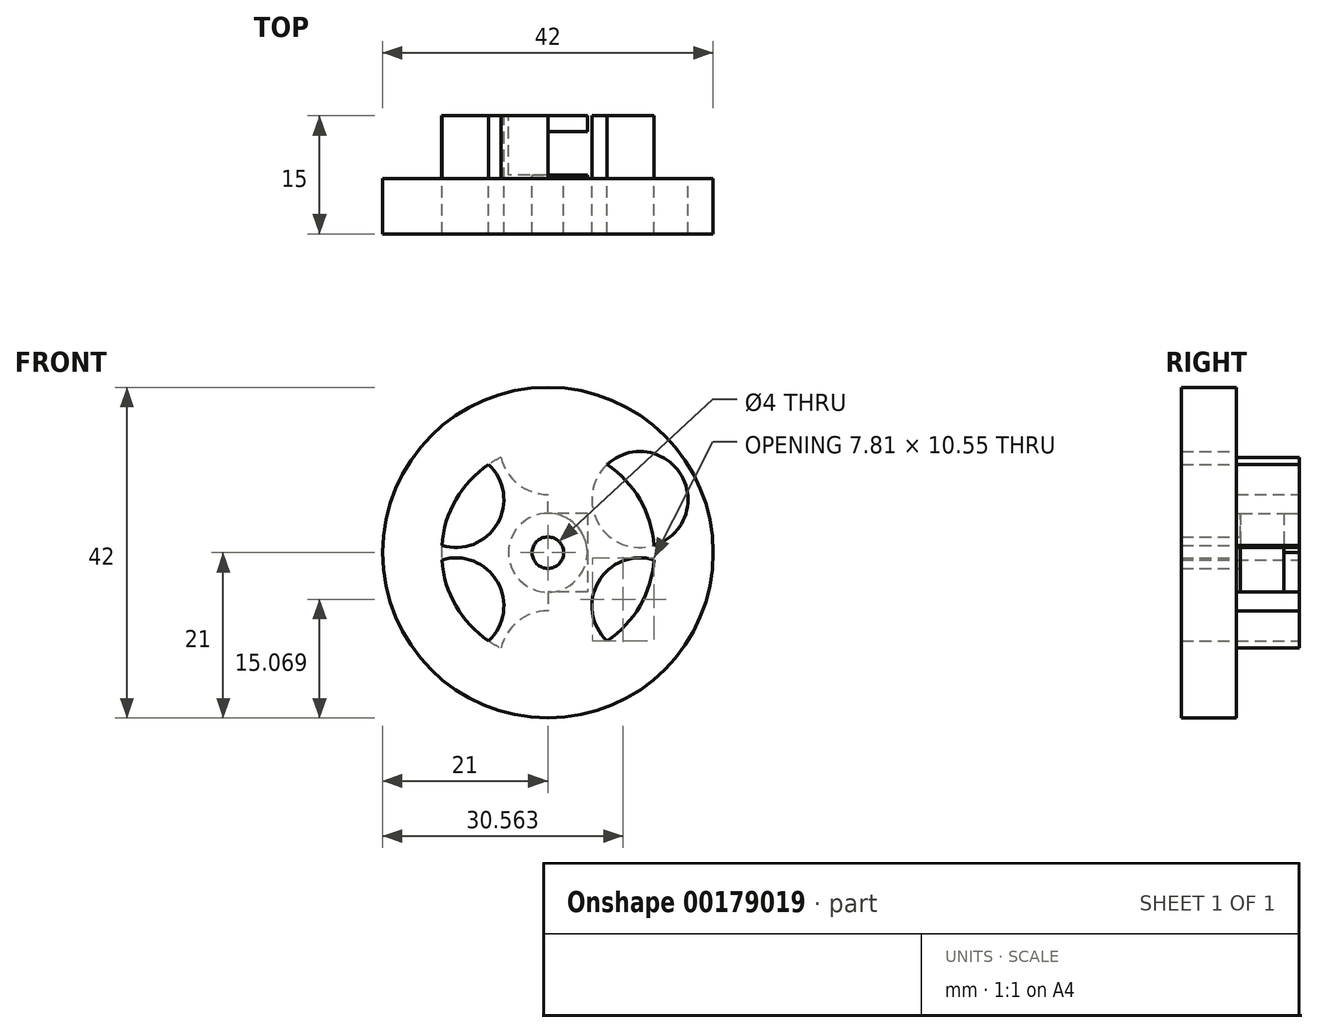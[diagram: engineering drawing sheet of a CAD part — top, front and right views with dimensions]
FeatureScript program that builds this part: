
annotation { "Feature Type Name" : "Feature", "Feature Type Description" : "" }
export const myFeature = defineFeature(function(context is Context, id is Id, definition is map)
    precondition{}
    {
        {
            var Q0;
            Q0=qCreatedBy(makeId("Front.planeOp"),FACE);
            var sketch = newSketch(context, id + "F0", { "sketchPlane" : qUnion([Q0])});
            skCircle(sketch, "E0", {"center": v(0, 0) * mm, "radius": 21 * mm});
            skCircle(sketch, "E1", {"center": v(0, 0) * mm, "radius": 13.5 * mm});
            skCircle(sketch, "E2", {"center": v(0, 13.5) * mm, "radius": 6.1 * mm});
            skLineSegment(sketch, "E3", {"start": v(0, 0) * mm, "end": v(0, 13.5) * mm});
            skLineSegment(sketch, "E4.3.0", {"start": v(0, 0) * mm, "end": v(0, -17.5) * mm});
            skCircle(sketch, "E5", {"center": v(0, 0) * mm, "radius": 5 * mm});
            skCircle(sketch, "E6.1.0", {"center": v(-11.7, 6.75) * mm, "radius": 6.1 * mm});
            skCircle(sketch, "E6.2.0", {"center": v(-11.7, -6.75) * mm, "radius": 6.1 * mm});
            skCircle(sketch, "E6.3.0", {"center": v(0, -13.5) * mm, "radius": 6.1 * mm});
            skCircle(sketch, "E6.4.0", {"center": v(11.7, -6.75) * mm, "radius": 6.1 * mm});
            skCircle(sketch, "E6.5.0", {"center": v(11.7, 6.75) * mm, "radius": 6.1 * mm});
            skSolve(sketch);
        }
        {
            var Q0;
            Q0=qSketchRegion(id+"F0",true);
            var Q1;
            {var subQ3=sQuery(id+"F0.wireOp",EDGE,"tZOFWktZ-ElV9-8rvC-aUia-Pu95TyRWtfmy");var subQ5=sQuery(id+"F0.wireOp",EDGE,"E1");var subQ6=makeQuery(id+"F0.imprint","INTERSECT",VERTEX,{"disambiguationData":[OD(1.0)],"derivedFrom":[subQ5,subQ3]});Q1=makeQuery(id+"F0.imprint","IMPRINT",FACE,{"disambiguationData":[TD([[makeQuery(id+"F0.imprint","IMPRINT",EDGE,{"disambiguationData":[TD([[subQ6,-1.0]])],"derivedFrom":subQ5}),1.0]])]});}
            var Q2;
            {var subQ3=sQuery(id+"F0.wireOp",EDGE,"KCc62wJ9-mbiY-6kxt-bQFC-ecyapfwqHlXu");var subQ5=sQuery(id+"F0.wireOp",EDGE,"E1");var subQ6=makeQuery(id+"F0.imprint","INTERSECT",VERTEX,{"disambiguationData":[OD(1.0)],"derivedFrom":[subQ5,subQ3]});Q2=makeQuery(id+"F0.imprint","IMPRINT",FACE,{"disambiguationData":[TD([[makeQuery(id+"F0.imprint","IMPRINT",EDGE,{"disambiguationData":[TD([[subQ6,-1.0]])],"derivedFrom":subQ5}),1.0]])]});}
            var Q3;
            {var subQ3=sQuery(id+"F0.wireOp",EDGE,"0Yy4USeo-LOO3-cS4v-iVgx-1SsoAEMeRNpn");var subQ5=sQuery(id+"F0.wireOp",EDGE,"E1");var subQ6=makeQuery(id+"F0.imprint","INTERSECT",VERTEX,{"disambiguationData":[OD(1.0)],"derivedFrom":[subQ5,subQ3]});Q3=makeQuery(id+"F0.imprint","IMPRINT",FACE,{"disambiguationData":[TD([[makeQuery(id+"F0.imprint","IMPRINT",EDGE,{"disambiguationData":[TD([[subQ6,-1.0]])],"derivedFrom":subQ5}),1.0]])]});}
            var Q4;
            {var subQ5=sQuery(id+"F0.wireOp",EDGE,"E1");var subQ7=sQuery(id+"F0.wireOp",EDGE,"54YZh0VT-RaSH-f3J3-LX5H-yRfJ3TOlvn7D");var subQ8=makeQuery(id+"F0.imprint","INTERSECT",VERTEX,{"disambiguationData":[OD(0.0)],"derivedFrom":[subQ5,subQ7]});Q4=makeQuery(id+"F0.imprint","IMPRINT",FACE,{"disambiguationData":[TD([[makeQuery(id+"F0.imprint","IMPRINT",EDGE,{"disambiguationData":[TD([[subQ8,-1.0]])],"derivedFrom":subQ5}),1.0]])]});}
            var Q5;
            {var subQ3=sQuery(id+"F0.wireOp",EDGE,"E2");var subQ6=sQuery(id+"F0.wireOp",EDGE,"E1");var subQ9=makeQuery(id+"F0.imprint","INTERSECT",VERTEX,{"disambiguationData":[OD(1.0)],"derivedFrom":[subQ6,subQ3]});Q5=makeQuery(id+"F0.imprint","IMPRINT",FACE,{"disambiguationData":[TD([[makeQuery(id+"F0.imprint","IMPRINT",EDGE,{"disambiguationData":[TD([[subQ9,-1.0]])],"derivedFrom":subQ6}),1.0]])]});}
            var Q6;
            {var subQ0=sQuery(id+"F0.wireOp",EDGE,"E1");var subQ1=makeQuery(id+"F0.imprint","INTERSECT",VERTEX,{"derivedFrom":[subQ0,sQuery(id+"F0.wireOp",EDGE,"E4.3.0")]});Q6=makeQuery(id+"F0.imprint","IMPRINT",FACE,{"disambiguationData":[TD([[makeQuery(id+"F0.imprint","IMPRINT",EDGE,{"disambiguationData":[TD([[subQ1,1.0]])],"derivedFrom":subQ0}),-1.0]])]});}
            var Q7;
            {var subQ0=sQuery(id+"F0.wireOp",EDGE,"E4.3.0");var subQ1=sQuery(id+"F0.wireOp",EDGE,"E1");var subQ2=makeQuery(id+"F0.imprint","INTERSECT",VERTEX,{"derivedFrom":[subQ1,subQ0]});Q7=makeQuery(id+"F0.imprint","IMPRINT",FACE,{"disambiguationData":[TD([[makeQuery(id+"F0.imprint","IMPRINT",EDGE,{"disambiguationData":[TD([[subQ2,-1.0]])],"derivedFrom":subQ1}),1.0]])]});}
            var Q8;
            {var subQ0=sQuery(id+"F0.wireOp",EDGE,"E4.3.0");var subQ1=sQuery(id+"F0.wireOp",EDGE,"E1");var subQ2=makeQuery(id+"F0.imprint","INTERSECT",VERTEX,{"derivedFrom":[subQ1,subQ0]});Q8=makeQuery(id+"F0.imprint","IMPRINT",FACE,{"disambiguationData":[TD([[makeQuery(id+"F0.imprint","IMPRINT",EDGE,{"disambiguationData":[TD([[subQ2,1.0]])],"derivedFrom":subQ1}),1.0]])]});}
            var Q9;
            {var subQ0=sQuery(id+"F0.wireOp",EDGE,"E6.4.0");var subQ1=sQuery(id+"F0.wireOp",EDGE,"E1");var subQ2=makeQuery(id+"F0.imprint","INTERSECT",VERTEX,{"disambiguationData":[OD(0.0)],"derivedFrom":[subQ1,subQ0]});Q9=makeQuery(id+"F0.imprint","IMPRINT",FACE,{"disambiguationData":[TD([[makeQuery(id+"F0.imprint","IMPRINT",EDGE,{"disambiguationData":[TD([[subQ2,-1.0]])],"derivedFrom":subQ1}),-1.0]])]});}
            var Q10;
            {var subQ0=sQuery(id+"F0.wireOp",EDGE,"E6.5.0");var subQ1=sQuery(id+"F0.wireOp",EDGE,"E1");var subQ16=makeQuery(id+"F0.imprint","INTERSECT",VERTEX,{"disambiguationData":[OD(0.0)],"derivedFrom":[subQ1,subQ0]});Q10=makeQuery(id+"F0.imprint","IMPRINT",FACE,{"disambiguationData":[TD([[makeQuery(id+"F0.imprint","IMPRINT",EDGE,{"disambiguationData":[TD([[subQ16,-1.0]])],"derivedFrom":subQ1}),1.0]])]});}
            var Q11;
            {var subQ0=sQuery(id+"F0.wireOp",EDGE,"E4.3.0");var subQ1=sQuery(id+"F0.wireOp",EDGE,"E3");var subQ2=makeQuery(id+"F0.imprint","INTERSECT",VERTEX,{"derivedFrom":[subQ1,subQ0]});Q11=makeQuery(id+"F0.imprint","IMPRINT",FACE,{"disambiguationData":[TD([[makeQuery(id+"F0.imprint","IMPRINT",EDGE,{"disambiguationData":[TD([[subQ2,-1.0]])],"derivedFrom":subQ1}),-1.0]])]});}
            var Q12;
            {var subQ0=sQuery(id+"F0.wireOp",EDGE,"E4.3.0");var subQ1=sQuery(id+"F0.wireOp",EDGE,"E3");var subQ2=makeQuery(id+"F0.imprint","INTERSECT",VERTEX,{"derivedFrom":[subQ1,subQ0]});Q12=makeQuery(id+"F0.imprint","IMPRINT",FACE,{"disambiguationData":[TD([[makeQuery(id+"F0.imprint","IMPRINT",EDGE,{"disambiguationData":[TD([[subQ2,-1.0]])],"derivedFrom":subQ1}),1.0]])]});}
            var Q13;
            {var subQ0=sQuery(id+"F0.wireOp",EDGE,"E6.2.0");var subQ1=sQuery(id+"F0.wireOp",EDGE,"E1");var subQ2=makeQuery(id+"F0.imprint","INTERSECT",VERTEX,{"disambiguationData":[OD(0.0)],"derivedFrom":[subQ1,subQ0]});Q13=makeQuery(id+"F0.imprint","IMPRINT",FACE,{"disambiguationData":[TD([[makeQuery(id+"F0.imprint","IMPRINT",EDGE,{"disambiguationData":[TD([[subQ2,-1.0]])],"derivedFrom":subQ1}),-1.0]])]});}
            var Q14;
            {var subQ0=sQuery(id+"F0.wireOp",EDGE,"E6.1.0");var subQ1=sQuery(id+"F0.wireOp",EDGE,"E1");var subQ2=makeQuery(id+"F0.imprint","INTERSECT",VERTEX,{"disambiguationData":[OD(0.0)],"derivedFrom":[subQ1,subQ0]});Q14=makeQuery(id+"F0.imprint","IMPRINT",FACE,{"disambiguationData":[TD([[makeQuery(id+"F0.imprint","IMPRINT",EDGE,{"disambiguationData":[TD([[subQ2,-1.0]])],"derivedFrom":subQ1}),-1.0]])]});}
            var Q15;
            {var subQ0=sQuery(id+"F0.wireOp",EDGE,"E1");var subQ1=makeQuery(id+"F0.imprint","INTERSECT",VERTEX,{"derivedFrom":[subQ0,sQuery(id+"F0.wireOp",EDGE,"E3")]});Q15=makeQuery(id+"F0.imprint","IMPRINT",FACE,{"disambiguationData":[TD([[makeQuery(id+"F0.imprint","IMPRINT",EDGE,{"disambiguationData":[TD([[subQ1,1.0]])],"derivedFrom":subQ0}),-1.0]])]});}
            var Q16;
            {var subQ0=sQuery(id+"F0.wireOp",EDGE,"E3");var subQ1=sQuery(id+"F0.wireOp",EDGE,"E1");var subQ2=makeQuery(id+"F0.imprint","INTERSECT",VERTEX,{"derivedFrom":[subQ1,subQ0]});Q16=makeQuery(id+"F0.imprint","IMPRINT",FACE,{"disambiguationData":[TD([[makeQuery(id+"F0.imprint","IMPRINT",EDGE,{"disambiguationData":[TD([[subQ2,-1.0]])],"derivedFrom":subQ1}),1.0]])]});}
            var Q17;
            {var subQ0=sQuery(id+"F0.wireOp",EDGE,"E3");var subQ1=sQuery(id+"F0.wireOp",EDGE,"E1");var subQ2=makeQuery(id+"F0.imprint","INTERSECT",VERTEX,{"derivedFrom":[subQ1,subQ0]});Q17=makeQuery(id+"F0.imprint","IMPRINT",FACE,{"disambiguationData":[TD([[makeQuery(id+"F0.imprint","IMPRINT",EDGE,{"disambiguationData":[TD([[subQ2,1.0]])],"derivedFrom":subQ1}),1.0]])]});}
            var Q18;
            {var subQ0=sQuery(id+"F0.wireOp",EDGE,"E6.5.0");var subQ1=sQuery(id+"F0.wireOp",EDGE,"E1");var subQ2=makeQuery(id+"F0.imprint","INTERSECT",VERTEX,{"disambiguationData":[OD(0.0)],"derivedFrom":[subQ1,subQ0]});Q18=makeQuery(id+"F0.imprint","IMPRINT",FACE,{"disambiguationData":[TD([[makeQuery(id+"F0.imprint","IMPRINT",EDGE,{"disambiguationData":[TD([[subQ2,1.0]])],"derivedFrom":subQ1}),1.0]])]});}
            var Q19;
            {var subQ0=sQuery(id+"F0.wireOp",EDGE,"E6.5.0");var subQ1=sQuery(id+"F0.wireOp",EDGE,"E1");var subQ2=makeQuery(id+"F0.imprint","INTERSECT",VERTEX,{"disambiguationData":[OD(0.0)],"derivedFrom":[subQ1,subQ0]});Q19=makeQuery(id+"F0.imprint","IMPRINT",FACE,{"disambiguationData":[TD([[makeQuery(id+"F0.imprint","IMPRINT",EDGE,{"disambiguationData":[TD([[subQ2,1.0]])],"derivedFrom":subQ1}),-1.0]])]});}
            extrude(context, id + "F1", {"entities" : qUnion([Q0, Q1, Q2, Q3, Q4, Q5, Q6, Q7, Q8, Q9, Q10, Q11, Q12, Q13, Q14, Q15, Q16, Q17, Q18, Q19]), "depth" : 15 * mm});
        }
        {
            var Q0;
            {var subQ0=sQuery(id+"F0.wireOp",EDGE,"E6.5.0");var subQ1=sQuery(id+"F0.wireOp",EDGE,"E1");var subQ2=makeQuery(id+"F0.imprint","INTERSECT",VERTEX,{"disambiguationData":[OD(0.0)],"derivedFrom":[subQ1,subQ0]});Q0=makeQuery(id+"F0.imprint","IMPRINT",FACE,{"disambiguationData":[TD([[makeQuery(id+"F0.imprint","IMPRINT",EDGE,{"disambiguationData":[TD([[subQ2,1.0]])],"derivedFrom":subQ1}),1.0]])]});}
            var Q1;
            {var subQ0=sQuery(id+"F0.wireOp",EDGE,"E6.5.0");var subQ1=sQuery(id+"F0.wireOp",EDGE,"E1");var subQ2=makeQuery(id+"F0.imprint","INTERSECT",VERTEX,{"disambiguationData":[OD(0.0)],"derivedFrom":[subQ1,subQ0]});Q1=makeQuery(id+"F0.imprint","IMPRINT",FACE,{"disambiguationData":[TD([[makeQuery(id+"F0.imprint","IMPRINT",EDGE,{"disambiguationData":[TD([[subQ2,1.0]])],"derivedFrom":subQ1}),-1.0]])]});}
            var Q2;
            {var subQ0=sQuery(id+"F0.wireOp",EDGE,"E6.4.0");var subQ1=sQuery(id+"F0.wireOp",EDGE,"E1");var subQ2=makeQuery(id+"F0.imprint","INTERSECT",VERTEX,{"disambiguationData":[OD(0.0)],"derivedFrom":[subQ1,subQ0]});Q2=makeQuery(id+"F0.imprint","IMPRINT",FACE,{"disambiguationData":[TD([[makeQuery(id+"F0.imprint","IMPRINT",EDGE,{"disambiguationData":[TD([[subQ2,-1.0]])],"derivedFrom":subQ1}),-1.0]])]});}
            var Q3;
            {var subQ0=sQuery(id+"F0.wireOp",EDGE,"E6.4.0");var subQ1=sQuery(id+"F0.wireOp",EDGE,"E1");var subQ2=makeQuery(id+"F0.imprint","INTERSECT",VERTEX,{"disambiguationData":[OD(0.0)],"derivedFrom":[subQ1,subQ0]});Q3=makeQuery(id+"F0.imprint","IMPRINT",FACE,{"disambiguationData":[TD([[makeQuery(id+"F0.imprint","IMPRINT",EDGE,{"disambiguationData":[TD([[subQ2,-1.0]])],"derivedFrom":subQ1}),1.0]])]});}
            var Q4;
            {var subQ0=sQuery(id+"F0.wireOp",EDGE,"E4.3.0");var subQ1=sQuery(id+"F0.wireOp",EDGE,"E1");var subQ2=makeQuery(id+"F0.imprint","INTERSECT",VERTEX,{"derivedFrom":[subQ1,subQ0]});Q4=makeQuery(id+"F0.imprint","IMPRINT",FACE,{"disambiguationData":[TD([[makeQuery(id+"F0.imprint","IMPRINT",EDGE,{"disambiguationData":[TD([[subQ2,-1.0]])],"derivedFrom":subQ1}),1.0]])]});}
            var Q5;
            {var subQ0=sQuery(id+"F0.wireOp",EDGE,"E1");var subQ1=makeQuery(id+"F0.imprint","INTERSECT",VERTEX,{"derivedFrom":[subQ0,sQuery(id+"F0.wireOp",EDGE,"E4.3.0")]});Q5=makeQuery(id+"F0.imprint","IMPRINT",FACE,{"disambiguationData":[TD([[makeQuery(id+"F0.imprint","IMPRINT",EDGE,{"disambiguationData":[TD([[subQ1,1.0]])],"derivedFrom":subQ0}),-1.0]])]});}
            var Q6;
            {var subQ0=sQuery(id+"F0.wireOp",EDGE,"E4.3.0");var subQ1=sQuery(id+"F0.wireOp",EDGE,"E1");var subQ2=makeQuery(id+"F0.imprint","INTERSECT",VERTEX,{"derivedFrom":[subQ1,subQ0]});Q6=makeQuery(id+"F0.imprint","IMPRINT",FACE,{"disambiguationData":[TD([[makeQuery(id+"F0.imprint","IMPRINT",EDGE,{"disambiguationData":[TD([[subQ2,1.0]])],"derivedFrom":subQ1}),1.0]])]});}
            var Q7;
            {var subQ0=sQuery(id+"F0.wireOp",EDGE,"E6.2.0");var subQ1=sQuery(id+"F0.wireOp",EDGE,"E1");var subQ2=makeQuery(id+"F0.imprint","INTERSECT",VERTEX,{"disambiguationData":[OD(0.0)],"derivedFrom":[subQ1,subQ0]});Q7=makeQuery(id+"F0.imprint","IMPRINT",FACE,{"disambiguationData":[TD([[makeQuery(id+"F0.imprint","IMPRINT",EDGE,{"disambiguationData":[TD([[subQ2,-1.0]])],"derivedFrom":subQ1}),1.0]])]});}
            var Q8;
            {var subQ0=sQuery(id+"F0.wireOp",EDGE,"E6.2.0");var subQ1=sQuery(id+"F0.wireOp",EDGE,"E1");var subQ2=makeQuery(id+"F0.imprint","INTERSECT",VERTEX,{"disambiguationData":[OD(0.0)],"derivedFrom":[subQ1,subQ0]});Q8=makeQuery(id+"F0.imprint","IMPRINT",FACE,{"disambiguationData":[TD([[makeQuery(id+"F0.imprint","IMPRINT",EDGE,{"disambiguationData":[TD([[subQ2,-1.0]])],"derivedFrom":subQ1}),-1.0]])]});}
            var Q9;
            {var subQ0=sQuery(id+"F0.wireOp",EDGE,"E6.1.0");var subQ1=sQuery(id+"F0.wireOp",EDGE,"E1");var subQ2=makeQuery(id+"F0.imprint","INTERSECT",VERTEX,{"disambiguationData":[OD(0.0)],"derivedFrom":[subQ1,subQ0]});Q9=makeQuery(id+"F0.imprint","IMPRINT",FACE,{"disambiguationData":[TD([[makeQuery(id+"F0.imprint","IMPRINT",EDGE,{"disambiguationData":[TD([[subQ2,-1.0]])],"derivedFrom":subQ1}),1.0]])]});}
            var Q10;
            {var subQ0=sQuery(id+"F0.wireOp",EDGE,"E6.1.0");var subQ1=sQuery(id+"F0.wireOp",EDGE,"E1");var subQ2=makeQuery(id+"F0.imprint","INTERSECT",VERTEX,{"disambiguationData":[OD(0.0)],"derivedFrom":[subQ1,subQ0]});Q10=makeQuery(id+"F0.imprint","IMPRINT",FACE,{"disambiguationData":[TD([[makeQuery(id+"F0.imprint","IMPRINT",EDGE,{"disambiguationData":[TD([[subQ2,-1.0]])],"derivedFrom":subQ1}),-1.0]])]});}
            var Q11;
            {var subQ0=sQuery(id+"F0.wireOp",EDGE,"E3");var subQ1=sQuery(id+"F0.wireOp",EDGE,"E1");var subQ2=makeQuery(id+"F0.imprint","INTERSECT",VERTEX,{"derivedFrom":[subQ1,subQ0]});Q11=makeQuery(id+"F0.imprint","IMPRINT",FACE,{"disambiguationData":[TD([[makeQuery(id+"F0.imprint","IMPRINT",EDGE,{"disambiguationData":[TD([[subQ2,-1.0]])],"derivedFrom":subQ1}),1.0]])]});}
            var Q12;
            {var subQ0=sQuery(id+"F0.wireOp",EDGE,"E3");var subQ1=sQuery(id+"F0.wireOp",EDGE,"E1");var subQ2=makeQuery(id+"F0.imprint","INTERSECT",VERTEX,{"derivedFrom":[subQ1,subQ0]});Q12=makeQuery(id+"F0.imprint","IMPRINT",FACE,{"disambiguationData":[TD([[makeQuery(id+"F0.imprint","IMPRINT",EDGE,{"disambiguationData":[TD([[subQ2,1.0]])],"derivedFrom":subQ1}),1.0]])]});}
            var Q13;
            {var subQ0=sQuery(id+"F0.wireOp",EDGE,"E1");var subQ1=makeQuery(id+"F0.imprint","INTERSECT",VERTEX,{"derivedFrom":[subQ0,sQuery(id+"F0.wireOp",EDGE,"E3")]});Q13=makeQuery(id+"F0.imprint","IMPRINT",FACE,{"disambiguationData":[TD([[makeQuery(id+"F0.imprint","IMPRINT",EDGE,{"disambiguationData":[TD([[subQ1,1.0]])],"derivedFrom":subQ0}),-1.0]])]});}
            extrude(context, id + "F2", {"entities" : qUnion([Q0, Q1, Q2, Q3, Q4, Q5, Q6, Q7, Q8, Q9, Q10, Q11, Q12, Q13]), "operationType" : NewBodyOperationType.REMOVE, "depth" : 8 * mm});
        }
        {
            var Q0;
            Q0=makeQuery(id+"F1.opExtrude","CAP_FACE",FACE,{"disambiguationData":[OSD([sQuery(id+"F0.wireOp",EDGE,"E0")])],"isStart":true});
            var sketch = newSketch(context, id + "F3", { "sketchPlane" : qUnion([Q0])});
            skLineSegment(sketch, "E7.bottom", {"start": v(-5, 5) * mm, "end": v(5, 5) * mm});
            skLineSegment(sketch, "E7.top", {"start": v(-5, -5) * mm, "end": v(5, -5) * mm});
            skLineSegment(sketch, "E7.left", {"start": v(-5, 5) * mm, "end": v(-5, -5) * mm});
            skLineSegment(sketch, "E7.right", {"start": v(5, 5) * mm, "end": v(5, -5) * mm});
            skPoint(sketch, "E7.middle", {"position": v(0, 0) * mm});
            skSolve(sketch);
        }
        {
            var Q0;
            Q0=makeQuery(id+"F1.opExtrude","CAP_FACE",FACE,{"disambiguationData":[OSD([sQuery(id+"F0.wireOp",EDGE,"E0")])],"isStart":false});
            var sketch = newSketch(context, id + "F4", { "sketchPlane" : qUnion([Q0])});
            skLineSegment(sketch, "E8", {"start": v(0, 0) * mm, "end": v(-15, 0) * mm});
            skCircle(sketch, "E9", {"center": v(-15, 0) * mm, "radius": 1.5 * mm});
            skCircle(sketch, "E10.1.0", {"center": v(0, -15) * mm, "radius": 1.5 * mm});
            skCircle(sketch, "E10.2.0", {"center": v(15, 0) * mm, "radius": 1.5 * mm});
            skCircle(sketch, "E10.3.0", {"center": v(0, 15) * mm, "radius": 1.5 * mm});
            skPoint(sketch, "E10.center", {"position": v(0, 0) * mm});
            skSolve(sketch);
        }
        {
            var Q0;
            Q0=makeQuery(id+"F3.imprint","IMPRINT",FACE,{"disambiguationData":[TD([[makeQuery(id+"F3.imprint","IMPRINT",EDGE,{"derivedFrom":sQuery(id+"F3.wireOp",EDGE,"E7.bottom")}),-1.0]])]});
            extrude(context, id + "F5", {"entities" : qUnion([Q0]), "operationType" : NewBodyOperationType.ADD, "oppositeDirection" : true, "depth" : 2 * mm});
        }
        {
            var Q0;
            Q0=makeQuery(id+"F1.opExtrude","CAP_FACE",FACE,{"disambiguationData":[OSD([sQuery(id+"F0.wireOp",EDGE,"E0")])],"isStart":true});
            var sketch = newSketch(context, id + "F6", { "sketchPlane" : qUnion([Q0])});
            skCircle(sketch, "E11", {"center": v(0, 0) * mm, "radius": 5 * mm});
            skSolve(sketch);
        }
        {
            var Q0;
            Q0=makeQuery(id+"F6.imprint","IMPRINT",FACE,{"disambiguationData":[TD([[makeQuery(id+"F6.imprint","IMPRINT",EDGE,{"derivedFrom":sQuery(id+"F6.wireOp",EDGE,"E11")}),1.0]])]});
            extrude(context, id + "F7", {"entities" : qUnion([Q0]), "operationType" : NewBodyOperationType.REMOVE, "oppositeDirection" : true, "depth" : 7.5 * mm});
        }
        {
            var Q0;
            Q0=sQuery(id+"F6.wireOp",VERTEX,"E11.center");
            var Q1;
            Q1=makeQuery(id+"F1.opExtrude","SWEPT_BODY",BODY,{"disambiguationData":[OSD([sQuery(id+"F0.wireOp",EDGE,"E0")])]});
            hole(context, id + "F8", {"style" : HoleStyle.SIMPLE, "endStyle" : HoleEndStyle.THROUGH, "holeDiameter" : 4 * mm, "locations" : qUnion([Q0]), "scope" : qUnion([Q1]), "isTappedThrough" : true});
        }
    });
